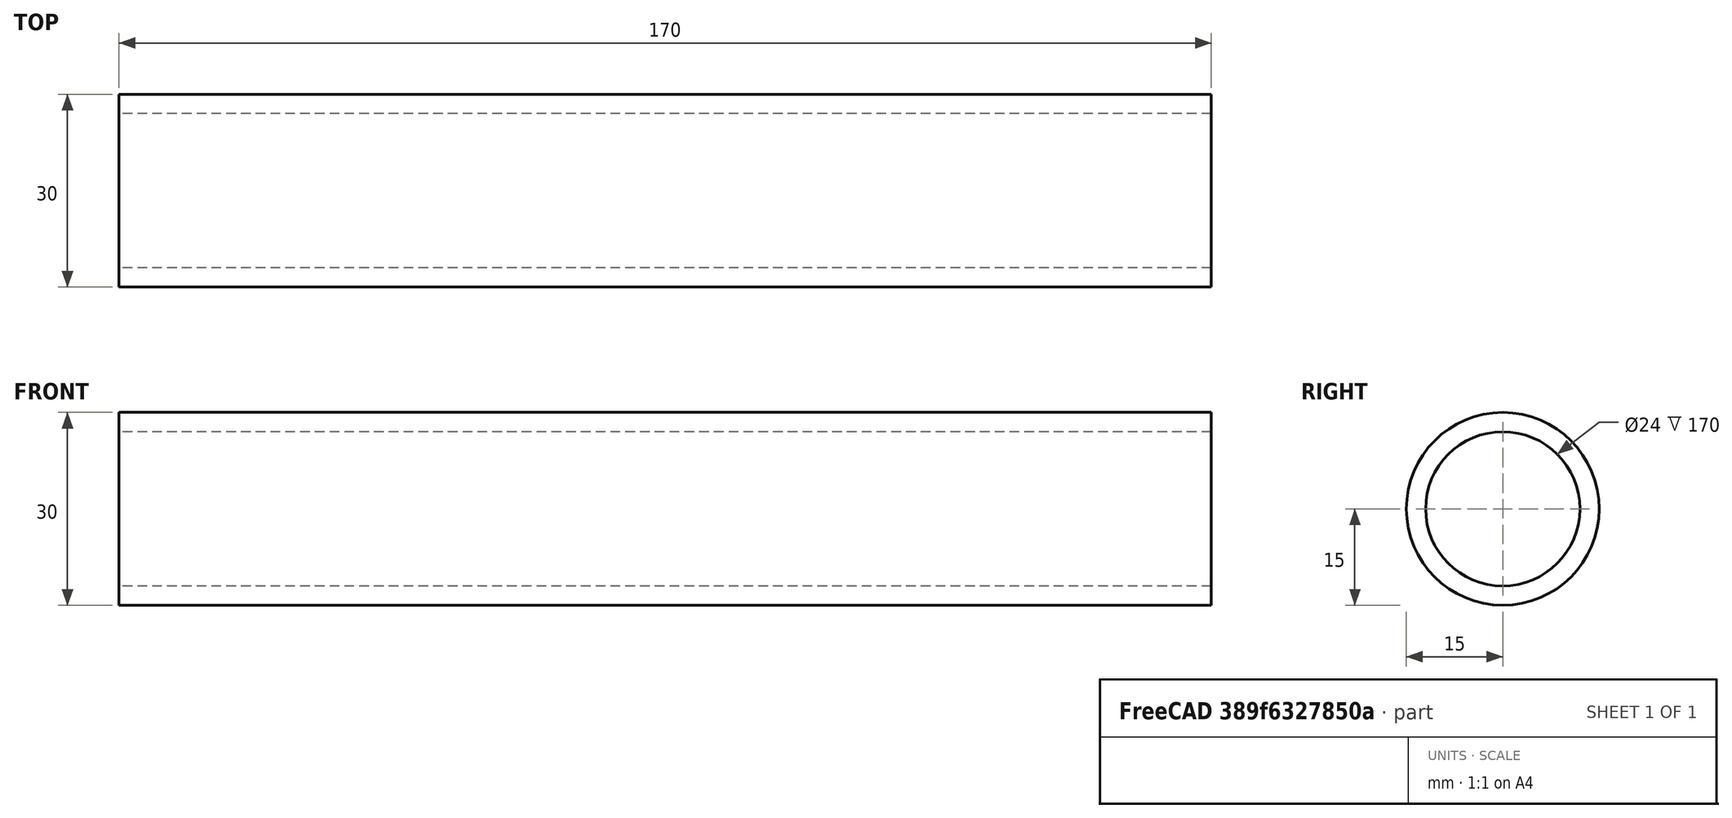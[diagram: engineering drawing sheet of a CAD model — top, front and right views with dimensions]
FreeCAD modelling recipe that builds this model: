
FCSTD DOCUMENT  (FreeCAD 0.19R)
Label: body
License: All rights reserved
LicenseURL: http://en.wikipedia.org/wiki/All_rights_reserved
objects: Sketcher::SketchObject×1, PartDesign::Revolution×1, PartDesign::Body×1
note: 4 computed .brp shape members not serialized (recipe doc carries the construction recipe); baked Part::Feature solids carry a one-line shape summary decoded from their .brp

FEATURE [Sketcher::SketchObject] Sketch
  MapMode = 5
  Support = -> [XY_Plane]
  sketch-geometry (4):
    g0: LineSegment StartX=0 StartY=15 StartZ=0 EndX=170 EndY=15 EndZ=0
    g1: LineSegment StartX=170 StartY=15 StartZ=0 EndX=170 EndY=12 EndZ=0
    g2: LineSegment StartX=170 StartY=12 StartZ=0 EndX=0 EndY=12 EndZ=0
    g3: LineSegment StartX=0 StartY=12 StartZ=0 EndX=0 EndY=15 EndZ=0
  constraints (12):
    c: Coincident(g2,g3)
    c: Coincident(g3,g0)
    c: Coincident(g0,g1)
    c: Coincident(g2,g1)
    c: Vertical(g1)
    c: Vertical(g3)
    c: Horizontal(g0)
    c: Horizontal(g2)
    c: Distance(g-1,g0) = 15
    c: Distance(g3) = 3
    c: Distance(g0) = 170
    c: PointOnObject(g2,g-2)
FEATURE [PartDesign::Revolution] Revolution
  AllowMultiFace = false
  Angle = 360
  Axis = (1,0,0)
  Base = (0,0,0)
  Profile = -> Sketch
  ReferenceAxis = -> Sketch [H_Axis]
FEATURE [PartDesign::Body] Body
  Group = -> [Sketch,Revolution]
  Origin = -> Origin
  Tip = -> Revolution
